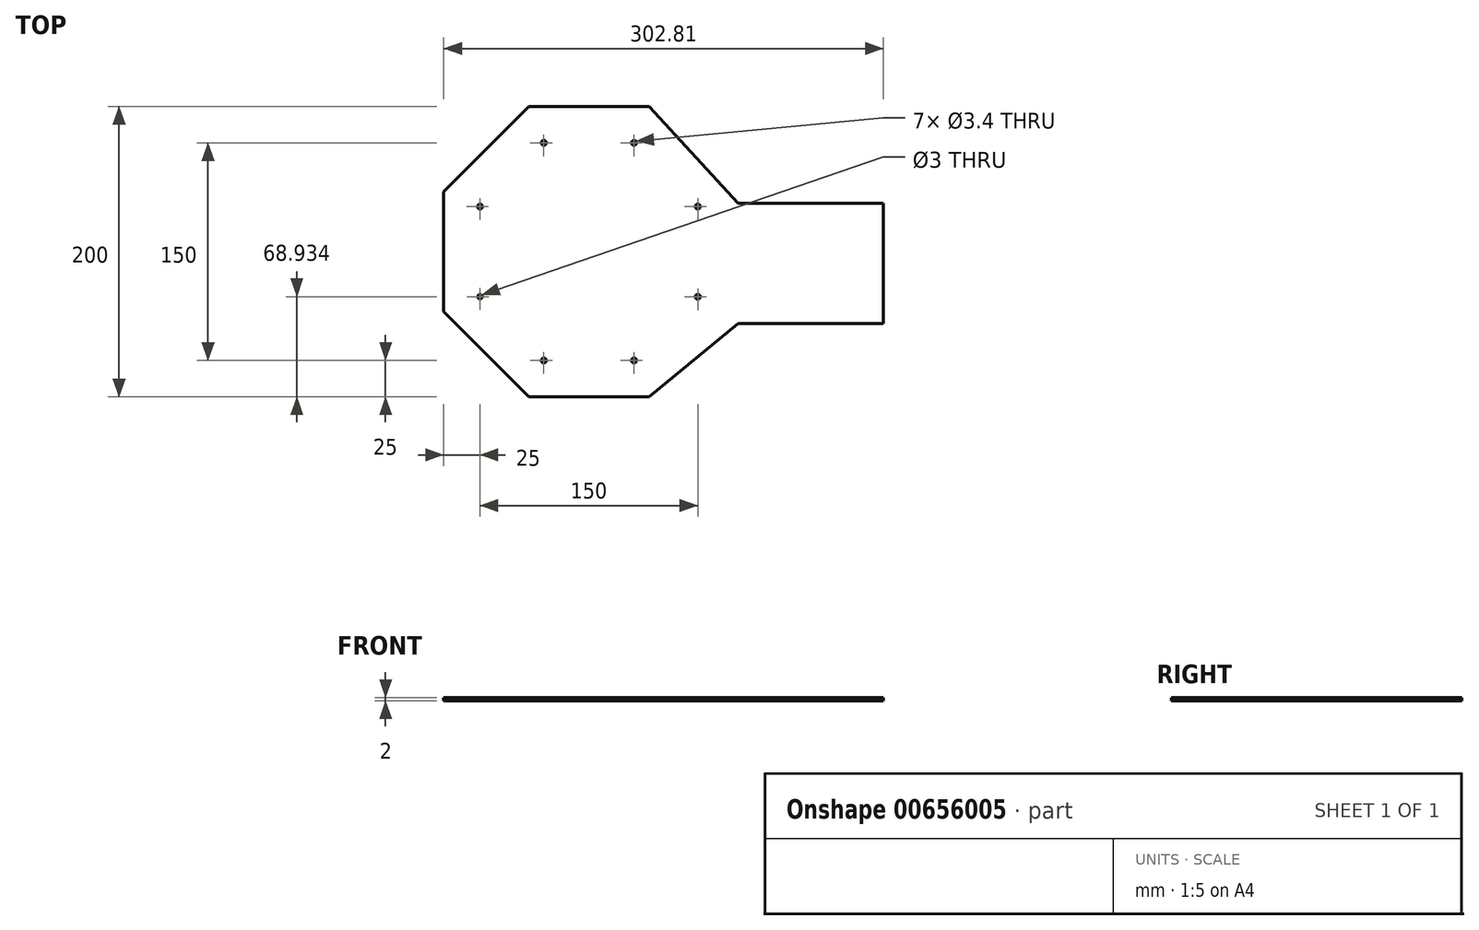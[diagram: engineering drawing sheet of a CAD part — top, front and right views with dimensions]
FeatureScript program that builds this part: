
annotation { "Feature Type Name" : "Feature", "Feature Type Description" : "" }
export const myFeature = defineFeature(function(context is Context, id is Id, definition is map)
    precondition{}
    {
        {
            var Q0;
            Q0=qCreatedBy(makeId("Top.planeOp"),FACE);
            var sketch = newSketch(context, id + "F0", { "sketchPlane" : qUnion([Q0])});
            skLineSegment(sketch, "E0.0", {"start": v(-41.42, 100) * mm, "end": v(41.42, 100) * mm});
            skLineSegment(sketch, "E0.1", {"start": v(41.42, 100) * mm, "end": v(102.8, 33.46) * mm});
            skLineSegment(sketch, "E0.3", {"start": v(102.8, -49.38) * mm, "end": v(41.42, -100) * mm});
            skLineSegment(sketch, "E0.4", {"start": v(41.42, -100) * mm, "end": v(-41.42, -100) * mm});
            skLineSegment(sketch, "E0.5", {"start": v(-41.42, -100) * mm, "end": v(-100, -41.42) * mm});
            skLineSegment(sketch, "E0.6", {"start": v(-100, -41.42) * mm, "end": v(-100, 41.42) * mm});
            skLineSegment(sketch, "E0.7", {"start": v(-100, 41.42) * mm, "end": v(-41.42, 100) * mm});
            skLineSegment(sketch, "E1.bottom", {"start": v(102.8, 33.46) * mm, "end": v(202.8, 33.46) * mm});
            skLineSegment(sketch, "E1.top", {"start": v(102.8, -49.38) * mm, "end": v(202.8, -49.38) * mm});
            skLineSegment(sketch, "E1.right", {"start": v(202.8, 33.46) * mm, "end": v(202.8, -49.38) * mm});
            skCircle(sketch, "E2", {"center": v(-31.07, 75) * mm, "radius": 1.7 * mm});
            skCircle(sketch, "E3", {"center": v(31.07, 75) * mm, "radius": 1.7 * mm});
            skCircle(sketch, "E4", {"center": v(75, 31.07) * mm, "radius": 1.7 * mm});
            skCircle(sketch, "E5", {"center": v(75, -31.07) * mm, "radius": 1.7 * mm});
            skCircle(sketch, "E6", {"center": v(31.07, -75) * mm, "radius": 1.7 * mm});
            skCircle(sketch, "E7", {"center": v(-31.07, -75) * mm, "radius": 1.7 * mm});
            skCircle(sketch, "E8", {"center": v(-75, -31.07) * mm, "radius": 1.5 * mm});
            skCircle(sketch, "E9", {"center": v(-75, 31.07) * mm, "radius": 1.7 * mm});
            skSolve(sketch);
        }
        {
            var Q0;
            Q0=makeQuery(id+"F0.imprint","IMPRINT",FACE,{"disambiguationData":[TD([[makeQuery(id+"F0.imprint","IMPRINT",EDGE,{"derivedFrom":sQuery(id+"F0.wireOp",EDGE,"E0.0")}),-1.0]])]});
            extrude(context, id + "F1", {"entities" : qUnion([Q0]), "depth" : 2 * mm, "offsetDistance" : 25 * mm});
        }
    });
